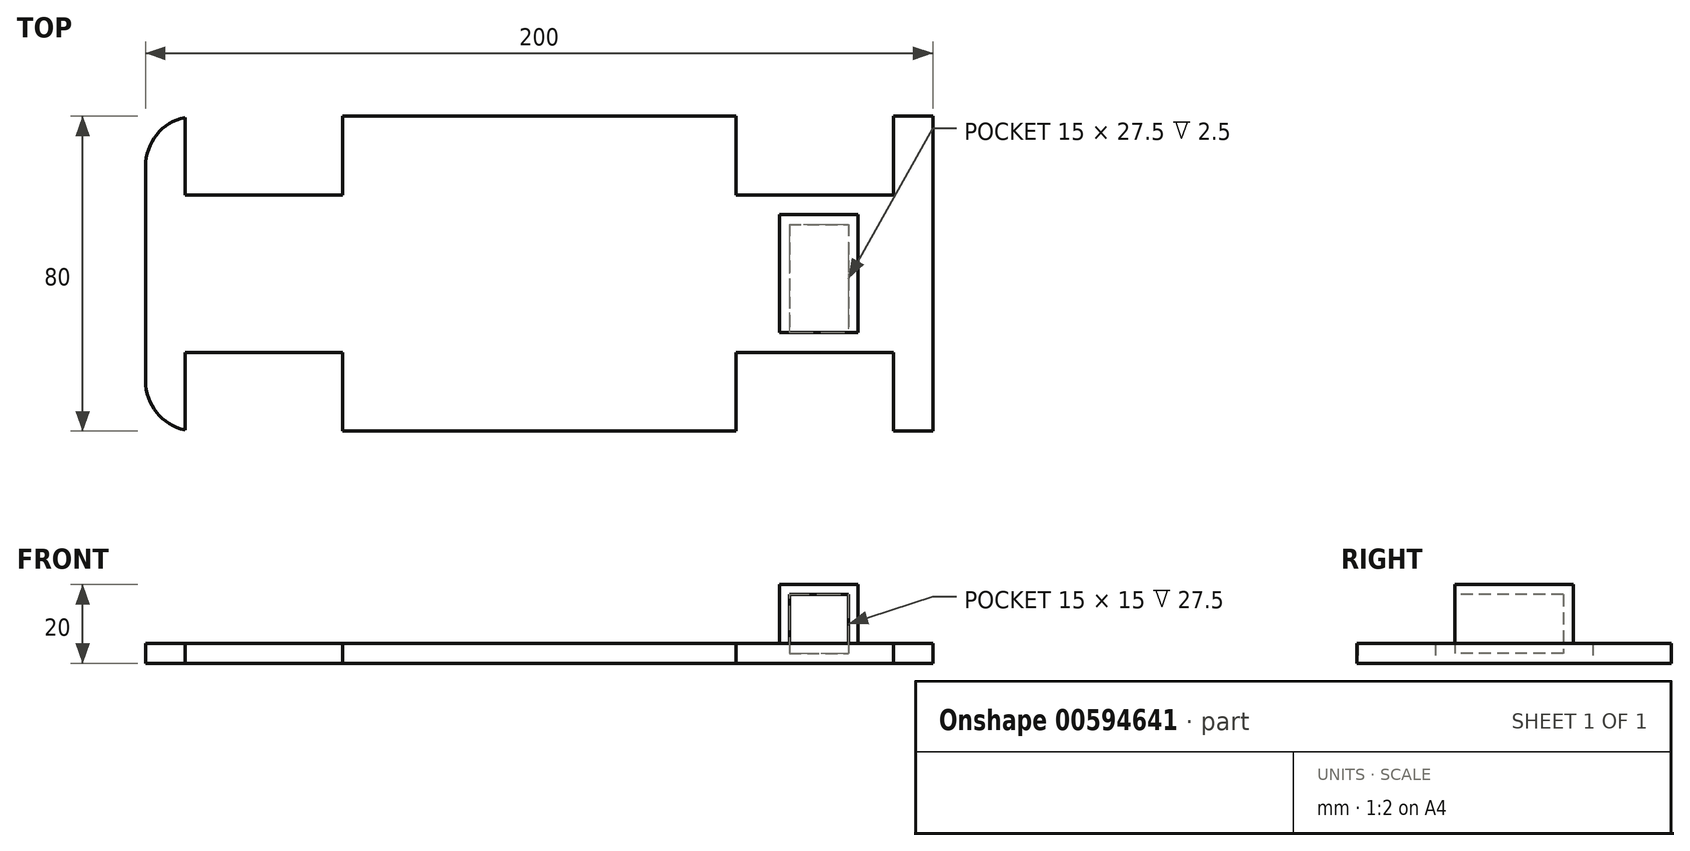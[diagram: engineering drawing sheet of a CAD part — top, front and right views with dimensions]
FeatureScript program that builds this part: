
annotation { "Feature Type Name" : "Feature", "Feature Type Description" : "" }
export const myFeature = defineFeature(function(context is Context, id is Id, definition is map)
    precondition{}
    {
        {
            var Q0;
            Q0=qCreatedBy(makeId("Top.planeOp"),FACE);
            var sketch = newSketch(context, id + "F0", { "sketchPlane" : qUnion([Q0])});
            skLineSegment(sketch, "E0.bottom", {"start": v(-100, 40) * mm, "end": v(-100, 40) * mm});
            skLineSegment(sketch, "E0.top", {"start": v(-100, -40) * mm, "end": v(-100, -40) * mm});
            skLineSegment(sketch, "E0.left", {"start": v(-100, 27.3) * mm, "end": v(-100, -27.3) * mm});
            skLineSegment(sketch, "E0.right", {"start": v(100, 40) * mm, "end": v(100, 40) * mm});
            skLineSegment(sketch, "E1", {"start": v(-50, 40) * mm, "end": v(-50, -40) * mm});
            skLineSegment(sketch, "E2", {"start": v(50, 40) * mm, "end": v(50, -40) * mm});
            skLineSegment(sketch, "E3", {"start": v(-50, 40) * mm, "end": v(50, 40) * mm});
            skLineSegment(sketch, "E4", {"start": v(-50, -40) * mm, "end": v(50, -40) * mm});
            skLineSegment(sketch, "E5", {"start": v(50, 40) * mm, "end": v(90, 40) * mm, "construction": true});
            skLineSegment(sketch, "E6", {"start": v(100, -40) * mm, "end": v(100, -40) * mm});
            skLineSegment(sketch, "E7", {"start": v(50, -40) * mm, "end": v(90, -40) * mm, "construction": true});
            skLineSegment(sketch, "E8", {"start": v(-100, 20) * mm, "end": v(-50, 20) * mm});
            skLineSegment(sketch, "E9", {"start": v(50, 20) * mm, "end": v(100, 20) * mm});
            skLineSegment(sketch, "E10", {"start": v(-90, 40) * mm, "end": v(-90, 40) * mm});
            skLineSegment(sketch, "E11", {"start": v(90, 40) * mm, "end": v(90, -40) * mm});
            skLineSegment(sketch, "E12", {"start": v(-90, 40) * mm, "end": v(-50, 40) * mm, "construction": true});
            skLineSegment(sketch, "E13", {"start": v(-90, 40) * mm, "end": v(-87.3, 40) * mm});
            skLineSegment(sketch, "E14", {"start": v(-90, -40) * mm, "end": v(-50, -40) * mm, "construction": true});
            skLineSegment(sketch, "E15", {"start": v(90, 40) * mm, "end": v(100, 40) * mm});
            skLineSegment(sketch, "E16", {"start": v(100, 40) * mm, "end": v(100, -40) * mm});
            skLineSegment(sketch, "E17", {"start": v(90, -40) * mm, "end": v(100, -40) * mm});
            skLineSegment(sketch, "E18", {"start": v(0, 0) * mm, "end": v(-100, 0) * mm, "construction": true});
            skLineSegment(sketch, "E19.MirrorCS", {"start": v(-100, -20) * mm, "end": v(-50, -20) * mm});
            skLineSegment(sketch, "E20.MirrorCS", {"start": v(-90, -40) * mm, "end": v(-87.3, -40) * mm});
            skLineSegment(sketch, "E21.MirrorCS", {"start": v(50, -20) * mm, "end": v(100, -20) * mm});
            skArc(sketch, "E22.filletArc", {"start": v(-100, -27.3) * mm, "mid": v(-97.19, -35.27) * mm, "end": v(-90, -39.7) * mm});
            skPoint(sketch, "E23.visualSharp", {"position": v(-100, 40) * mm});
            skLineSegment(sketch, "E23.filletArc", {"start": v(-87.3, 40) * mm, "end": v(-87.3, 40) * mm});
            skArc(sketch, "E24", {"start": v(-87.3, 40) * mm, "mid": v(-88.66, 39.93) * mm, "end": v(-90, 39.7) * mm, "construction": true});
            skArc(sketch, "E25", {"start": v(-90, 39.7) * mm, "mid": v(-97.19, 35.27) * mm, "end": v(-100, 27.3) * mm});
            skLineSegment(sketch, "E26", {"start": v(-90, 39.7) * mm, "end": v(-90, -39.7) * mm});
            skLineSegment(sketch, "E27", {"start": v(-90, 40) * mm, "end": v(-90, 39.7) * mm, "construction": true});
            skLineSegment(sketch, "E28", {"start": v(-90, -20) * mm, "end": v(-90, -39.7) * mm});
            skArc(sketch, "E29", {"start": v(-90, -39.7) * mm, "mid": v(-88.66, -39.93) * mm, "end": v(-87.3, -40) * mm, "construction": true});
            skLineSegment(sketch, "E30", {"start": v(-87.3, -40) * mm, "end": v(-87.3, -40) * mm});
            skPoint(sketch, "E31.middle", {"position": v(50, 0) * mm});
            skPoint(sketch, "E32.middle", {"position": v(0, 0) * mm});
            skLineSegment(sketch, "E33.bottom", {"start": v(61.05, 15) * mm, "end": v(81.05, 15) * mm});
            skLineSegment(sketch, "E33.top", {"start": v(61.05, -15) * mm, "end": v(81.05, -15) * mm});
            skLineSegment(sketch, "E33.left", {"start": v(61.05, 15) * mm, "end": v(61.05, -15) * mm});
            skLineSegment(sketch, "E33.right", {"start": v(81.05, 15) * mm, "end": v(81.05, -15) * mm});
            skPoint(sketch, "E33.middle", {"position": v(71.05, 0) * mm});
            skSolve(sketch);
        }
        {
            var Q0;
            Q0=makeQuery(id+"F0.imprint","IMPRINT",FACE,{"disambiguationData":[TD([[makeQuery(id+"F0.imprint","IMPRINT",EDGE,{"derivedFrom":sQuery(id+"F0.wireOp",EDGE,"E33.bottom")}),-1.0]])]});
            extrude(context, id + "F1", {"entities" : qUnion([Q0]), "depth" : 20 * mm, "offsetDistance" : 25.4 * mm});
        }
        {
            var Q0;
            {var subQ0=sQuery(id+"F0.wireOp",EDGE,"E25");Q0=makeQuery(id+"F0.imprint","IMPRINT",FACE,{"disambiguationData":[TD([[makeQuery(id+"F0.imprint","IMPRINT",EDGE,{"derivedFrom":subQ0}),1.0]])]});}
            var Q1;
            {var subQ0=sQuery(id+"F0.wireOp",EDGE,"E8");var subQ1=sQuery(id+"F0.wireOp",EDGE,"E0.left");var subQ2=makeQuery(id+"F0.imprint","INTERSECT",VERTEX,{"derivedFrom":[subQ1,subQ0]});Q1=makeQuery(id+"F0.imprint","IMPRINT",FACE,{"disambiguationData":[TD([[makeQuery(id+"F0.imprint","IMPRINT",EDGE,{"disambiguationData":[TD([[subQ2,-1.0]])],"derivedFrom":subQ1}),1.0]])]});}
            var Q2;
            {var subQ0=sQuery(id+"F0.wireOp",EDGE,"E22.filletArc");Q2=makeQuery(id+"F0.imprint","IMPRINT",FACE,{"disambiguationData":[TD([[makeQuery(id+"F0.imprint","IMPRINT",EDGE,{"derivedFrom":subQ0}),1.0]])]});}
            var Q3;
            {var subQ0=sQuery(id+"F0.wireOp",EDGE,"E8");var subQ1=sQuery(id+"F0.wireOp",EDGE,"E1");var subQ2=makeQuery(id+"F0.imprint","INTERSECT",VERTEX,{"derivedFrom":[subQ1,subQ0]});Q3=makeQuery(id+"F0.imprint","IMPRINT",FACE,{"disambiguationData":[TD([[makeQuery(id+"F0.imprint","IMPRINT",EDGE,{"disambiguationData":[TD([[subQ2,-1.0]])],"derivedFrom":subQ1}),-1.0]])]});}
            var Q4;
            {var subQ0=sQuery(id+"F0.wireOp",EDGE,"E3");Q4=makeQuery(id+"F0.imprint","IMPRINT",FACE,{"disambiguationData":[TD([[makeQuery(id+"F0.imprint","IMPRINT",EDGE,{"derivedFrom":subQ0}),-1.0]])]});}
            var Q5;
            Q5=makeQuery(id+"F0.imprint","IMPRINT",FACE,{"disambiguationData":[TD([[makeQuery(id+"F0.imprint","IMPRINT",EDGE,{"derivedFrom":sQuery(id+"F0.wireOp",EDGE,"E33.bottom")}),1.0]])]});
            var Q6;
            {var subQ0=sQuery(id+"F0.wireOp",EDGE,"E16");var subQ1=sQuery(id+"F0.wireOp",EDGE,"E9");var subQ2=makeQuery(id+"F0.imprint","INTERSECT",VERTEX,{"derivedFrom":[subQ1,subQ0]});Q6=makeQuery(id+"F0.imprint","IMPRINT",FACE,{"disambiguationData":[TD([[makeQuery(id+"F0.imprint","IMPRINT",EDGE,{"disambiguationData":[TD([[subQ2,1.0]])],"derivedFrom":subQ1}),-1.0]])]});}
            var Q7;
            {var subQ0=sQuery(id+"F0.wireOp",EDGE,"E17");Q7=makeQuery(id+"F0.imprint","IMPRINT",FACE,{"disambiguationData":[TD([[makeQuery(id+"F0.imprint","IMPRINT",EDGE,{"derivedFrom":subQ0}),1.0]])]});}
            var Q8;
            {var subQ5=sQuery(id+"F0.wireOp",EDGE,"E15");Q8=makeQuery(id+"F0.imprint","IMPRINT",FACE,{"disambiguationData":[TD([[makeQuery(id+"F0.imprint","IMPRINT",EDGE,{"derivedFrom":subQ5}),-1.0]])]});}
            extrude(context, id + "F2", {"entities" : qUnion([Q0, Q1, Q2, Q3, Q4, Q5, Q6, Q7, Q8]), "operationType" : NewBodyOperationType.ADD, "depth" : 5 * mm, "offsetDistance" : 25.4 * mm});
        }
        {
            var Q0;
            Q0=makeQuery(id+"F1.opExtrude","SWEPT_FACE",FACE,{"disambiguationData":[OSD([sQuery(id+"F0.wireOp",EDGE,"E33.top")])]});
            shell(context, id + "F3", {"entities" : qUnion([Q0]), "thickness" : 2.5 * mm});
        }
    });
